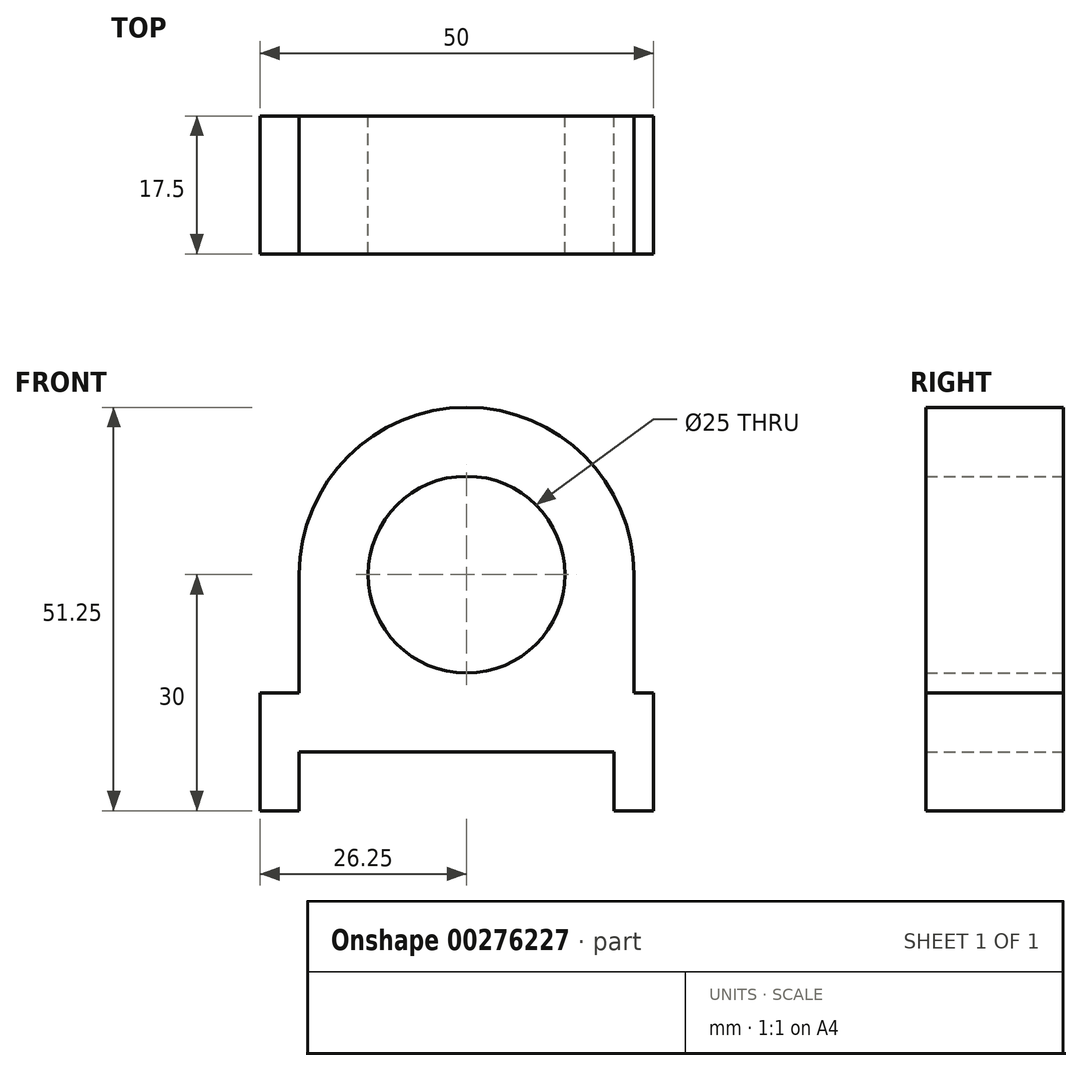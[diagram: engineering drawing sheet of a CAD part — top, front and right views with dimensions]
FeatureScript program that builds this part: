
annotation { "Feature Type Name" : "Feature", "Feature Type Description" : "" }
export const myFeature = defineFeature(function(context is Context, id is Id, definition is map)
    precondition{}
    {
        {
            var Q0;
            Q0=qCreatedBy(makeId("Front.planeOp"),FACE);
            var sketch = newSketch(context, id + "F0", { "sketchPlane" : qUnion([Q0])});
            skLineSegment(sketch, "E0", {"start": v(0, 0) * mm, "end": v(-5, 0) * mm});
            skLineSegment(sketch, "E1", {"start": v(-45, 0) * mm, "end": v(-50, 0) * mm});
            skLineSegment(sketch, "E2", {"start": v(-50, 0) * mm, "end": v(-50, 15) * mm});
            skLineSegment(sketch, "E3", {"start": v(-50, 15) * mm, "end": v(-45, 15) * mm});
            skLineSegment(sketch, "E4", {"start": v(-2.5, 30) * mm, "end": v(-2.5, 15) * mm});
            skLineSegment(sketch, "E5", {"start": v(-2.5, 15) * mm, "end": v(0, 15) * mm});
            skLineSegment(sketch, "E6", {"start": v(0, 15) * mm, "end": v(0, 0) * mm});
            skLineSegment(sketch, "E7", {"start": v(-45, 15) * mm, "end": v(-45, 30) * mm});
            skArc(sketch, "E8", {"start": v(-2.5, 30) * mm, "mid": v(-23.75, 51.25) * mm, "end": v(-45, 30) * mm});
            skPoint(sketch, "E9.start.orphan", {"position": v(-45, -12.5) * mm});
            skPoint(sketch, "E10.end.orphan", {"position": v(-2.5, -12.5) * mm});
            skLineSegment(sketch, "E11", {"start": v(-45, 0) * mm, "end": v(-45, 7.5) * mm});
            skPoint(sketch, "E11.endSnap0", {"position": v(-50, 7.5) * mm});
            skLineSegment(sketch, "E12", {"start": v(-45, 7.5) * mm, "end": v(-5, 7.5) * mm});
            skLineSegment(sketch, "E13", {"start": v(-5, 7.5) * mm, "end": v(-5, 0) * mm});
            skCircle(sketch, "E14", {"center": v(-23.75, 30) * mm, "radius": 12.5 * mm});
            skSolve(sketch);
        }
        {
            var Q0;
            Q0=makeQuery(id+"F0.imprint","IMPRINT",FACE,{"disambiguationData":[TD([[makeQuery(id+"F0.imprint","IMPRINT",EDGE,{"derivedFrom":sQuery(id+"F0.wireOp",EDGE,"E0")}),-1.0]])]});
            extrude(context, id + "F1", {"entities" : qUnion([Q0]), "depth" : 17.5 * mm});
        }
    });
